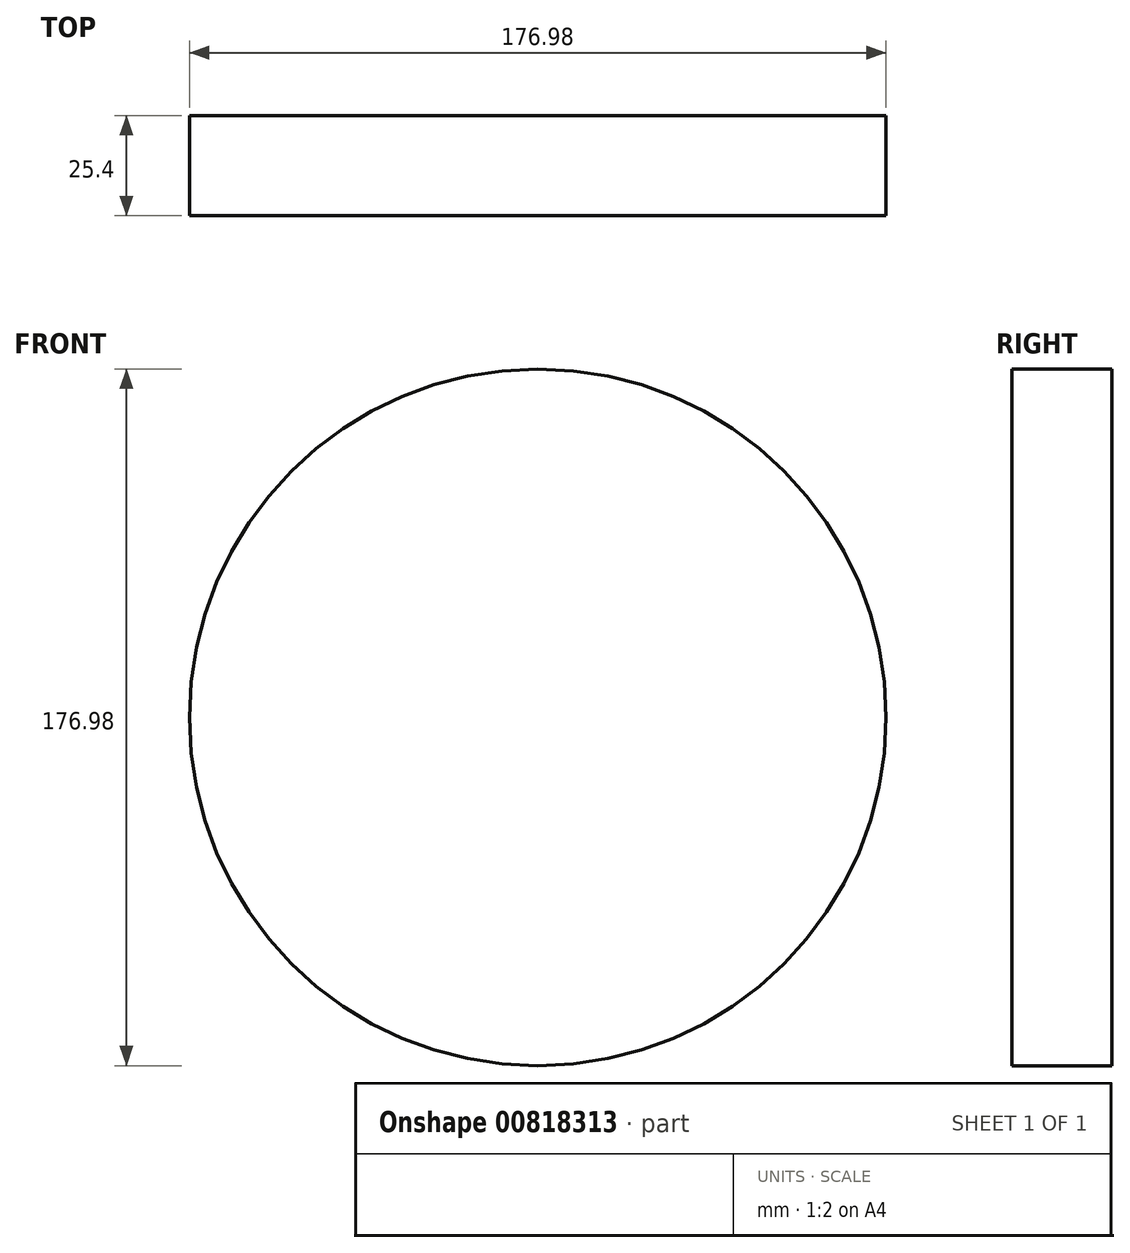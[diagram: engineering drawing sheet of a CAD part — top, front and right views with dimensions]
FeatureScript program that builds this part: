
annotation { "Feature Type Name" : "Feature", "Feature Type Description" : "" }
export const myFeature = defineFeature(function(context is Context, id is Id, definition is map)
    precondition{}
    {
        {
            var Q0;
            Q0=qCreatedBy(makeId("Front.planeOp"),FACE);
            var sketch = newSketch(context, id + "F0", { "sketchPlane" : qUnion([Q0])});
            skCircle(sketch, "E0", {"center": v(0, 0) * mm, "radius": 88.5 * mm});
            skSolve(sketch);
        }
        {
            var Q0;
            Q0=makeQuery(id+"F0.imprint","IMPRINT",FACE,{"disambiguationData":[TD([[makeQuery(id+"F0.imprint","IMPRINT",EDGE,{"derivedFrom":sQuery(id+"F0.wireOp",EDGE,"E0")}),1.0]])]});
            extrude(context, id + "F1", {"entities" : qUnion([Q0]), "depth" : 25.4 * mm, "offsetDistance" : 25.4 * mm});
        }
    });
